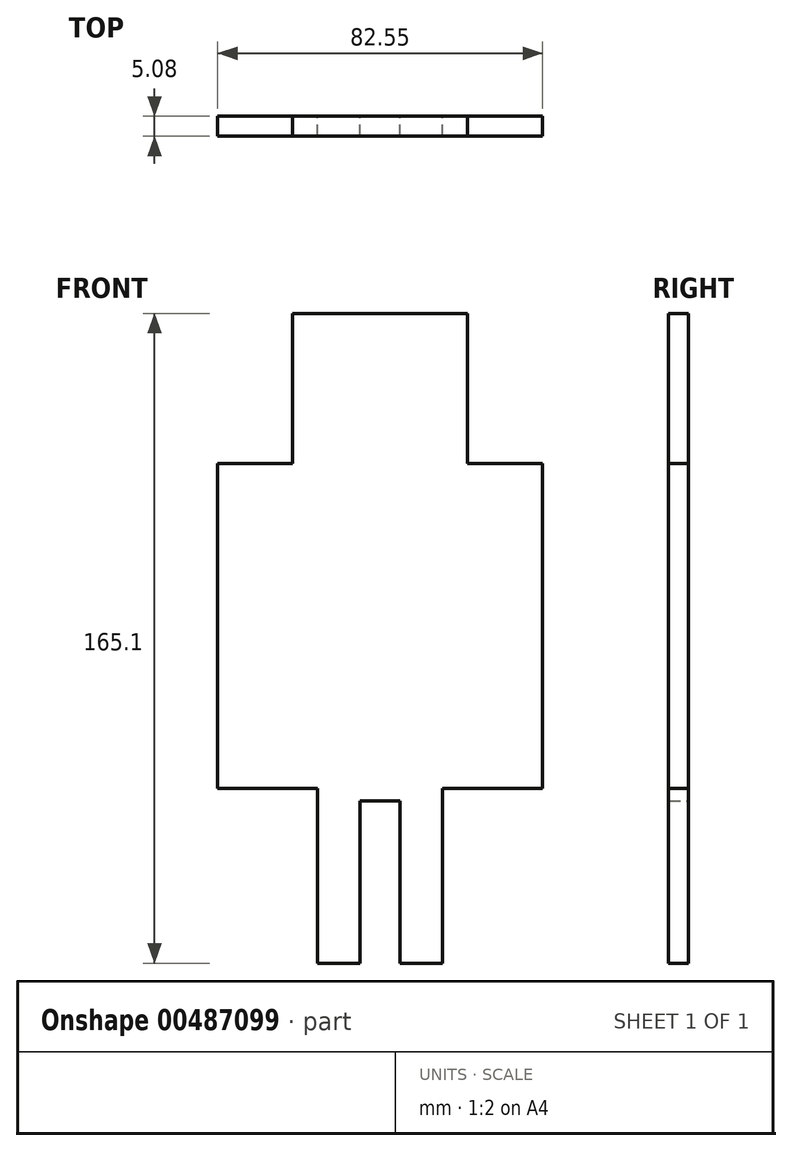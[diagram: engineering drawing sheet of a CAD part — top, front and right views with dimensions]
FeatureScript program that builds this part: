
annotation { "Feature Type Name" : "Feature", "Feature Type Description" : "" }
export const myFeature = defineFeature(function(context is Context, id is Id, definition is map)
    precondition{}
    {
        {
            var Q0;
            Q0=qCreatedBy(makeId("Front.planeOp"),FACE);
            var sketch = newSketch(context, id + "F0", { "sketchPlane" : qUnion([Q0])});
            skLineSegment(sketch, "E0.bottom", {"start": v(-14.71, 72.17) * mm, "end": v(29.74, 72.17) * mm});
            skLineSegment(sketch, "E0.top", {"start": v(-8.36, -92.93) * mm, "end": v(2.43, -92.93) * mm});
            skLineSegment(sketch, "E0.left", {"start": v(-33.76, 34.07) * mm, "end": v(-33.76, -48.48) * mm});
            skLineSegment(sketch, "E0.right", {"start": v(48.79, 34.07) * mm, "end": v(48.79, -48.48) * mm});
            skLineSegment(sketch, "E1.top", {"start": v(29.74, 34.07) * mm, "end": v(48.79, 34.07) * mm});
            skLineSegment(sketch, "E1.left", {"start": v(29.74, 72.17) * mm, "end": v(29.74, 34.07) * mm});
            skLineSegment(sketch, "E2.top", {"start": v(-14.71, 34.07) * mm, "end": v(-33.76, 34.07) * mm});
            skLineSegment(sketch, "E2.left", {"start": v(-14.71, 72.17) * mm, "end": v(-14.71, 34.07) * mm});
            skLineSegment(sketch, "E3.bottom", {"start": v(-33.76, -48.48) * mm, "end": v(-8.36, -48.48) * mm});
            skLineSegment(sketch, "E3.right", {"start": v(-8.36, -48.48) * mm, "end": v(-8.36, -92.93) * mm});
            skLineSegment(sketch, "E4.bottom", {"start": v(48.79, -48.48) * mm, "end": v(23.39, -48.48) * mm});
            skLineSegment(sketch, "E4.right", {"start": v(23.39, -48.48) * mm, "end": v(23.39, -92.93) * mm});
            skPoint(sketch, "E5.start.orphan", {"position": v(7.51, -92.93) * mm});
            skLineSegment(sketch, "E6.left", {"start": v(-8.36, -92.93) * mm, "end": v(-8.36, -51.65) * mm});
            skLineSegment(sketch, "E6.right", {"start": v(2.43, -92.93) * mm, "end": v(2.43, -51.65) * mm});
            skLineSegment(sketch, "E7.bottom", {"start": v(23.39, -92.93) * mm, "end": v(12.6, -92.93) * mm});
            skLineSegment(sketch, "E7.left", {"start": v(23.39, -92.93) * mm, "end": v(23.39, -51.65) * mm});
            skLineSegment(sketch, "E7.right", {"start": v(12.6, -92.93) * mm, "end": v(12.6, -51.65) * mm});
            skLineSegment(sketch, "E8", {"start": v(2.43, -51.65) * mm, "end": v(12.6, -51.65) * mm});
            skLineSegment(sketch, "E9.trimOffspring", {"start": v(12.6, -92.93) * mm, "end": v(23.39, -92.93) * mm});
            skSolve(sketch);
        }
        {
            var Q0;
            Q0 = qSketchRegion(id + "F0", true);
            extrude(context, id + "F1", {"entities" : qUnion([Q0]), "depth" : 5.08 * mm});
        }
    });
